# Revit family: Shower-Valve_Trim-KOHLER-STRAYT-K-37336T_1
name_source: partatom
category: Specialty Equipment
revit_build: Autodesk Revit 2017 (Build: 20160225_1515(x64)
units: mm (PartAtom-declared; Revit-internal decimal feet)

## family parameters
Cut with Voids When Loaded = No
Host = Face
OmniClass Number = 23.31.25.00
OmniClass Title = Toilet and Bath Specialties
Part Type = Normal
Room Calculation Point = No
Round Connector Dimension = Use Diameter
Shared = No

## types (3) — shared parameters
ADA Compliant = No
Assembly Code = C1030200
Date Modified = 05/21/2021
Default Elevation = 42"
Description = 40 mm in-wall shower panel
Finish = Kohler-Metal-CP-Polished_Chrome
Handle Clearance = 3 1/4"
Height = 6 9/16"
Length = 3 1/16"
Manufacturer = KOHLER Co.
Master Format 2014 = 10 28 00
Master Format 2014 Name = Toilet, Bath, and Laundry Accessories
Material = Premium Metal Construction
Product Documentation Link = https://files.kohler.com.cn
Product Name = STRAYT
Product Page URL = https://www.kohler.com.cn
URL = http://www.kohler.com.cn
WaterSense Certified = No
Width = 5 5/16"

## per-type parameters (varying)
| type | 4 | 4DPR | 4DPW | Model | Type |
| White Surface, CP-Polished Chrome | No | No | Yes | K-37336T-4DPW-CP | 1 |
| Red Surface, CP-Polished Chrome | No | Yes | No | K-37336T-4DPR-CP | 2 |
| CP-Polished Chrome | Yes | No | No | K-37336T-4-CP | 3 |

## geometry (parser evidence)
native form markers: Sweep x4
no freeform markers — native parametric forms only
